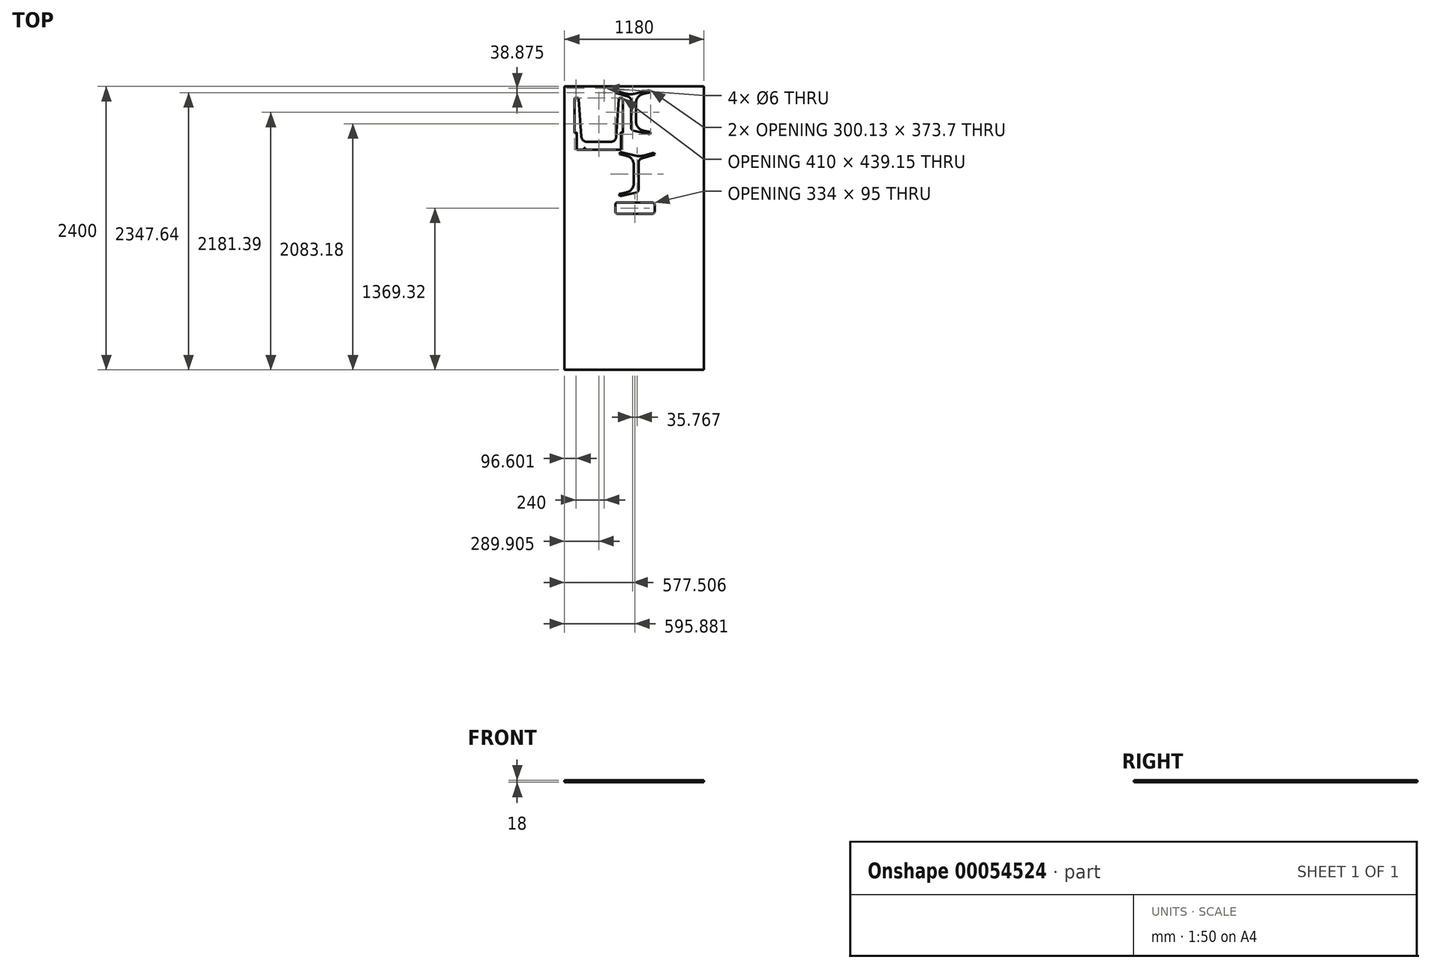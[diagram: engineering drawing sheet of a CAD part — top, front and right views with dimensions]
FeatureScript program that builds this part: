
annotation { "Feature Type Name" : "Feature", "Feature Type Description" : "" }
export const myFeature = defineFeature(function(context is Context, id is Id, definition is map)
    precondition{}
    {
        {
            var Q0;
            Q0=qCreatedBy(makeId("Top.planeOp"),FACE);
            var sketch = newSketch(context, id + "F0", { "sketchPlane" : qUnion([Q0])});
            skArc(sketch, "E0", {"start": v(-2548.4, 1578.94) * mm, "mid": v(-2545.76, 1572.58) * mm, "end": v(-2539.4, 1569.94) * mm});
            skLineSegment(sketch, "E1", {"start": v(-2539.4, 1569.94) * mm, "end": v(-2521.82, 1569.94) * mm});
            skArc(sketch, "E2", {"start": v(-2521.82, 1569.94) * mm, "mid": v(-2515.67, 1572.37) * mm, "end": v(-2512.84, 1578.34) * mm});
            skLineSegment(sketch, "E3", {"start": v(-2512.84, 1578.34) * mm, "end": v(-2491.59, 1896.94) * mm});
            skArc(sketch, "E4", {"start": v(-2491.59, 1896.94) * mm, "mid": v(-2476.37, 1929.04) * mm, "end": v(-2443.33, 1942.1) * mm});
            skLineSegment(sketch, "E5", {"start": v(-2443.33, 1942.1) * mm, "end": v(-2343.4, 1942.1) * mm});
            skLineSegment(sketch, "E6", {"start": v(-2343.4, 1942.1) * mm, "end": v(-2243.47, 1942.1) * mm});
            skArc(sketch, "E7", {"start": v(-2243.47, 1942.1) * mm, "mid": v(-2210.43, 1929.04) * mm, "end": v(-2195.21, 1896.94) * mm});
            skLineSegment(sketch, "E8", {"start": v(-2195.21, 1896.94) * mm, "end": v(-2173.96, 1578.34) * mm});
            skArc(sketch, "E9", {"start": v(-2173.96, 1578.34) * mm, "mid": v(-2171.13, 1572.37) * mm, "end": v(-2164.98, 1569.94) * mm});
            skLineSegment(sketch, "E10", {"start": v(-2164.98, 1569.94) * mm, "end": v(-2147.4, 1569.94) * mm});
            skArc(sketch, "E11", {"start": v(-2147.4, 1569.94) * mm, "mid": v(-2141.03, 1572.58) * mm, "end": v(-2138.4, 1578.94) * mm});
            skLineSegment(sketch, "E12", {"start": v(-2138.4, 1578.94) * mm, "end": v(-2138.4, 1864.94) * mm});
            skLineSegment(sketch, "E13", {"start": v(-2138.4, 1864.94) * mm, "end": v(-2150.74, 1864.94) * mm});
            skArc(sketch, "E14", {"start": v(-2150.74, 1864.94) * mm, "mid": v(-2156.4, 1864.94) * mm, "end": v(-2156.4, 1870.6) * mm});
            skLineSegment(sketch, "E15", {"start": v(-2156.4, 1870.6) * mm, "end": v(-2156.4, 2009.1) * mm});
            skLineSegment(sketch, "E16", {"start": v(-2156.4, 2009.1) * mm, "end": v(-2530.4, 2009.1) * mm});
            skLineSegment(sketch, "E17", {"start": v(-2530.4, 2009.1) * mm, "end": v(-2530.4, 1870.6) * mm});
            skArc(sketch, "E18", {"start": v(-2530.4, 1870.6) * mm, "mid": v(-2530.4, 1864.94) * mm, "end": v(-2536.06, 1864.94) * mm});
            skLineSegment(sketch, "E19", {"start": v(-2536.06, 1864.94) * mm, "end": v(-2548.4, 1864.94) * mm});
            skLineSegment(sketch, "E20", {"start": v(-2548.4, 1864.94) * mm, "end": v(-2548.4, 1578.94) * mm});
            skCircle(sketch, "E21", {"center": v(-1886.18, 1415.07) * mm, "radius": 3 * mm});
            skCircle(sketch, "E22", {"center": v(-2003.5, 1109.65) * mm, "radius": 3 * mm});
            skCircle(sketch, "E23", {"center": v(-1818.83, 1434.38) * mm, "radius": 3 * mm});
            skCircle(sketch, "E24", {"center": v(-2003.5, 1424.41) * mm, "radius": 3 * mm});
            skCircle(sketch, "E25", {"center": v(-1943.68, 1144.84) * mm, "radius": 3 * mm});
            skCircle(sketch, "E26", {"center": v(-2069.06, 1439.55) * mm, "radius": 3 * mm});
            skCircle(sketch, "E27", {"center": v(-1943.68, 1356.02) * mm, "radius": 3 * mm});
            skCircle(sketch, "E28", {"center": v(-2069.06, 1094.52) * mm, "radius": 3 * mm});
            skArc(sketch, "E29", {"start": v(-1949.68, 1112.84) * mm, "mid": v(-1938.52, 1119.88) * mm, "end": v(-1934.18, 1132.33) * mm});
            skLineSegment(sketch, "E30", {"start": v(-1934.18, 1132.33) * mm, "end": v(-1934.18, 1361.8) * mm});
            skArc(sketch, "E31", {"start": v(-1934.18, 1361.8) * mm, "mid": v(-1926.12, 1385.87) * mm, "end": v(-1905.2, 1400.25) * mm});
            skLineSegment(sketch, "E32", {"start": v(-1905.2, 1400.25) * mm, "end": v(-1796.66, 1431.37) * mm});
            skLineSegment(sketch, "E33", {"start": v(-1796.66, 1431.37) * mm, "end": v(-1801.62, 1448.68) * mm});
            skLineSegment(sketch, "E34", {"start": v(-1801.62, 1448.68) * mm, "end": v(-1883.4, 1425.23) * mm});
            skArc(sketch, "E35", {"start": v(-1883.4, 1425.23) * mm, "mid": v(-1920.82, 1419.47) * mm, "end": v(-1958.49, 1423.26) * mm});
            skLineSegment(sketch, "E36", {"start": v(-1958.49, 1423.26) * mm, "end": v(-2089.54, 1453.52) * mm});
            skLineSegment(sketch, "E37", {"start": v(-2089.54, 1453.52) * mm, "end": v(-2093.58, 1435.98) * mm});
            skLineSegment(sketch, "E38", {"start": v(-2093.58, 1435.98) * mm, "end": v(-2036.18, 1422.72) * mm});
            skArc(sketch, "E39", {"start": v(-2036.18, 1422.72) * mm, "mid": v(-1991.57, 1394.58) * mm, "end": v(-1974.18, 1344.77) * mm});
            skLineSegment(sketch, "E40", {"start": v(-1974.18, 1344.77) * mm, "end": v(-1974.18, 1189.3) * mm});
            skArc(sketch, "E41", {"start": v(-1974.18, 1189.3) * mm, "mid": v(-1991.57, 1139.5) * mm, "end": v(-2036.18, 1111.34) * mm});
            skLineSegment(sketch, "E42", {"start": v(-2036.18, 1111.34) * mm, "end": v(-2096.8, 1097.35) * mm});
            skLineSegment(sketch, "E43", {"start": v(-2096.8, 1097.35) * mm, "end": v(-2092.74, 1079.81) * mm});
            skLineSegment(sketch, "E44", {"start": v(-2092.74, 1079.81) * mm, "end": v(-1949.68, 1112.84) * mm});
            skLineSegment(sketch, "E45", {"start": v(-2203.5, 942.03) * mm, "end": v(-2186, 942.03) * mm});
            skLineSegment(sketch, "E46", {"start": v(-2186, 942.03) * mm, "end": v(-2186, 1249.22) * mm});
            skArc(sketch, "E47", {"start": v(-2186, 1249.22) * mm, "mid": v(-2194.79, 1270.43) * mm, "end": v(-2216, 1279.22) * mm});
            skLineSegment(sketch, "E48", {"start": v(-2216, 1279.22) * mm, "end": v(-2530, 1279.22) * mm});
            skArc(sketch, "E49", {"start": v(-2530, 1279.22) * mm, "mid": v(-2551.21, 1270.43) * mm, "end": v(-2560, 1249.22) * mm});
            skLineSegment(sketch, "E50", {"start": v(-2560, 1249.22) * mm, "end": v(-2560, 942.03) * mm});
            skLineSegment(sketch, "E51", {"start": v(-2560, 942.03) * mm, "end": v(-2542.5, 942.03) * mm});
            skArc(sketch, "E52", {"start": v(-2542.5, 942.03) * mm, "mid": v(-2540.38, 941.15) * mm, "end": v(-2539.5, 939.03) * mm});
            skLineSegment(sketch, "E53", {"start": v(-2539.5, 939.03) * mm, "end": v(-2539.5, 919.22) * mm});
            skArc(sketch, "E54", {"start": v(-2539.5, 919.22) * mm, "mid": v(-2533.64, 905.08) * mm, "end": v(-2519.5, 899.22) * mm});
            skLineSegment(sketch, "E55", {"start": v(-2519.5, 899.22) * mm, "end": v(-2226.5, 899.22) * mm});
            skArc(sketch, "E56", {"start": v(-2226.5, 899.22) * mm, "mid": v(-2212.36, 905.08) * mm, "end": v(-2206.5, 919.22) * mm});
            skLineSegment(sketch, "E57", {"start": v(-2206.5, 919.22) * mm, "end": v(-2206.5, 939.03) * mm});
            skArc(sketch, "E58", {"start": v(-2206.5, 939.03) * mm, "mid": v(-2205.62, 941.15) * mm, "end": v(-2203.5, 942.03) * mm});
            skLineSegment(sketch, "E59", {"start": v(-2131.12, 1005.82) * mm, "end": v(-2131.12, 950.82) * mm});
            skArc(sketch, "E60", {"start": v(-2131.12, 950.82) * mm, "mid": v(-2125.26, 936.68) * mm, "end": v(-2111.12, 930.82) * mm});
            skLineSegment(sketch, "E61", {"start": v(-2111.12, 930.82) * mm, "end": v(-1817.12, 930.82) * mm});
            skArc(sketch, "E62", {"start": v(-1817.12, 930.82) * mm, "mid": v(-1802.98, 936.68) * mm, "end": v(-1797.12, 950.82) * mm});
            skLineSegment(sketch, "E63", {"start": v(-1797.12, 950.82) * mm, "end": v(-1797.12, 1005.82) * mm});
            skArc(sketch, "E64", {"start": v(-1797.12, 1005.82) * mm, "mid": v(-1802.98, 1019.96) * mm, "end": v(-1817.12, 1025.82) * mm});
            skLineSegment(sketch, "E65", {"start": v(-1817.12, 1025.82) * mm, "end": v(-2111.12, 1025.82) * mm});
            skArc(sketch, "E66", {"start": v(-2111.12, 1025.82) * mm, "mid": v(-2125.26, 1019.96) * mm, "end": v(-2131.12, 1005.82) * mm});
            skLineSegment(sketch, "E67", {"start": v(-2507, 1456.47) * mm, "end": v(-2491.55, 1389.58) * mm});
            skLineSegment(sketch, "E68", {"start": v(-2491.55, 1389.58) * mm, "end": v(-2218.96, 1389.58) * mm});
            skLineSegment(sketch, "E69", {"start": v(-2218.96, 1389.58) * mm, "end": v(-2203.52, 1456.47) * mm});
            skLineSegment(sketch, "E70", {"start": v(-2203.52, 1456.47) * mm, "end": v(-2213.65, 1458.8) * mm});
            skArc(sketch, "E71", {"start": v(-2213.65, 1458.8) * mm, "mid": v(-2219.1, 1458.43) * mm, "end": v(-2223.44, 1455.07) * mm});
            skLineSegment(sketch, "E72", {"start": v(-2223.44, 1455.07) * mm, "end": v(-2245.43, 1424) * mm});
            skArc(sketch, "E73", {"start": v(-2245.43, 1424) * mm, "mid": v(-2253.38, 1417.07) * mm, "end": v(-2263.62, 1414.58) * mm});
            skLineSegment(sketch, "E74", {"start": v(-2263.62, 1414.58) * mm, "end": v(-2355.26, 1414.58) * mm});
            skLineSegment(sketch, "E75", {"start": v(-2355.26, 1414.58) * mm, "end": v(-2446.9, 1414.58) * mm});
            skArc(sketch, "E76", {"start": v(-2446.9, 1414.58) * mm, "mid": v(-2457.13, 1417.07) * mm, "end": v(-2465.08, 1424) * mm});
            skLineSegment(sketch, "E77", {"start": v(-2465.08, 1424) * mm, "end": v(-2487.08, 1455.07) * mm});
            skArc(sketch, "E78", {"start": v(-2487.08, 1455.07) * mm, "mid": v(-2491.4, 1458.43) * mm, "end": v(-2496.87, 1458.8) * mm});
            skLineSegment(sketch, "E79", {"start": v(-2496.87, 1458.8) * mm, "end": v(-2507, 1456.47) * mm});
            skArc(sketch, "E80", {"start": v(-1979.54, 1636.57) * mm, "mid": v(-1990.7, 1643.6) * mm, "end": v(-1995.05, 1656.05) * mm});
            skLineSegment(sketch, "E81", {"start": v(-1995.05, 1656.05) * mm, "end": v(-1995.05, 1885.52) * mm});
            skArc(sketch, "E82", {"start": v(-1995.05, 1885.52) * mm, "mid": v(-2003.1, 1909.6) * mm, "end": v(-2024.02, 1923.97) * mm});
            skLineSegment(sketch, "E83", {"start": v(-2024.02, 1923.97) * mm, "end": v(-2132.56, 1955.1) * mm});
            skLineSegment(sketch, "E84", {"start": v(-2132.56, 1955.1) * mm, "end": v(-2127.6, 1972.4) * mm});
            skLineSegment(sketch, "E85", {"start": v(-2127.6, 1972.4) * mm, "end": v(-2045.82, 1948.95) * mm});
            skArc(sketch, "E86", {"start": v(-2045.82, 1948.95) * mm, "mid": v(-2008.4, 1943.2) * mm, "end": v(-1970.73, 1946.98) * mm});
            skLineSegment(sketch, "E87", {"start": v(-1970.73, 1946.98) * mm, "end": v(-1839.69, 1977.24) * mm});
            skLineSegment(sketch, "E88", {"start": v(-1839.69, 1977.24) * mm, "end": v(-1835.64, 1959.7) * mm});
            skLineSegment(sketch, "E89", {"start": v(-1835.64, 1959.7) * mm, "end": v(-1893.04, 1946.45) * mm});
            skArc(sketch, "E90", {"start": v(-1893.04, 1946.45) * mm, "mid": v(-1937.65, 1918.3) * mm, "end": v(-1955.05, 1868.5) * mm});
            skLineSegment(sketch, "E91", {"start": v(-1955.05, 1868.5) * mm, "end": v(-1955.05, 1713.02) * mm});
            skArc(sketch, "E92", {"start": v(-1955.05, 1713.02) * mm, "mid": v(-1937.65, 1663.22) * mm, "end": v(-1893.04, 1635.07) * mm});
            skLineSegment(sketch, "E93", {"start": v(-1893.04, 1635.07) * mm, "end": v(-1832.43, 1621.07) * mm});
            skLineSegment(sketch, "E94", {"start": v(-1832.43, 1621.07) * mm, "end": v(-1836.48, 1603.54) * mm});
            skLineSegment(sketch, "E95", {"start": v(-1836.48, 1603.54) * mm, "end": v(-1979.54, 1636.57) * mm});
            skCircle(sketch, "E96", {"center": v(-1860.16, 1963.27) * mm, "radius": 3 * mm});
            skCircle(sketch, "E97", {"center": v(-1925.73, 1948.14) * mm, "radius": 3 * mm});
            skCircle(sketch, "E98", {"center": v(-2110.4, 1958.1) * mm, "radius": 3 * mm});
            skCircle(sketch, "E99", {"center": v(-1985.55, 1879.74) * mm, "radius": 3 * mm});
            skCircle(sketch, "E100", {"center": v(-1985.55, 1668.56) * mm, "radius": 3 * mm});
            skCircle(sketch, "E101", {"center": v(-1925.73, 1633.38) * mm, "radius": 3 * mm});
            skCircle(sketch, "E102", {"center": v(-1860.16, 1618.24) * mm, "radius": 3 * mm});
            skCircle(sketch, "E103", {"center": v(-2043.04, 1938.8) * mm, "radius": 3 * mm});
            skCircle(sketch, "E104", {"center": v(-2223.4, 1956.64) * mm, "radius": 3 * mm});
            skCircle(sketch, "E105", {"center": v(-2463.4, 1995.52) * mm, "radius": 3 * mm});
            skCircle(sketch, "E106", {"center": v(-2463.4, 1956.64) * mm, "radius": 3 * mm});
            skCircle(sketch, "E107", {"center": v(-2223.4, 1995.52) * mm, "radius": 3 * mm});
            skCircle(sketch, "E108", {"center": v(-2390.1, 1486.18) * mm, "radius": 3 * mm});
            skCircle(sketch, "E109", {"center": v(-2150.1, 1525.06) * mm, "radius": 3 * mm});
            skCircle(sketch, "E110", {"center": v(-2150.1, 1486.18) * mm, "radius": 3 * mm});
            skCircle(sketch, "E111", {"center": v(-2390.1, 1525.06) * mm, "radius": 3 * mm});
            skArc(sketch, "E112", {"start": v(-2065.1, 1902.75) * mm, "mid": v(-2067.73, 1909.12) * mm, "end": v(-2074.1, 1911.75) * mm});
            skLineSegment(sketch, "E113", {"start": v(-2074.1, 1911.75) * mm, "end": v(-2091.68, 1911.75) * mm});
            skArc(sketch, "E114", {"start": v(-2091.68, 1911.75) * mm, "mid": v(-2097.82, 1909.33) * mm, "end": v(-2100.66, 1903.35) * mm});
            skLineSegment(sketch, "E115", {"start": v(-2100.66, 1903.35) * mm, "end": v(-2121.9, 1584.75) * mm});
            skArc(sketch, "E116", {"start": v(-2121.9, 1584.75) * mm, "mid": v(-2137.12, 1552.65) * mm, "end": v(-2170.16, 1539.6) * mm});
            skLineSegment(sketch, "E117", {"start": v(-2170.16, 1539.6) * mm, "end": v(-2270.1, 1539.6) * mm});
            skLineSegment(sketch, "E118", {"start": v(-2270.1, 1539.6) * mm, "end": v(-2370.03, 1539.6) * mm});
            skArc(sketch, "E119", {"start": v(-2370.03, 1539.6) * mm, "mid": v(-2403.07, 1552.65) * mm, "end": v(-2418.28, 1584.75) * mm});
            skLineSegment(sketch, "E120", {"start": v(-2418.28, 1584.75) * mm, "end": v(-2439.53, 1903.35) * mm});
            skArc(sketch, "E121", {"start": v(-2439.53, 1903.35) * mm, "mid": v(-2442.37, 1909.33) * mm, "end": v(-2448.51, 1911.75) * mm});
            skLineSegment(sketch, "E122", {"start": v(-2448.51, 1911.75) * mm, "end": v(-2466.1, 1911.75) * mm});
            skArc(sketch, "E123", {"start": v(-2466.1, 1911.75) * mm, "mid": v(-2472.46, 1909.12) * mm, "end": v(-2475.1, 1902.75) * mm});
            skLineSegment(sketch, "E124", {"start": v(-2475.1, 1902.75) * mm, "end": v(-2475.1, 1616.76) * mm});
            skLineSegment(sketch, "E125", {"start": v(-2475.1, 1616.76) * mm, "end": v(-2462.75, 1616.76) * mm});
            skArc(sketch, "E126", {"start": v(-2462.75, 1616.76) * mm, "mid": v(-2457.1, 1616.76) * mm, "end": v(-2457.1, 1611.1) * mm});
            skLineSegment(sketch, "E127", {"start": v(-2457.1, 1611.1) * mm, "end": v(-2457.1, 1472.6) * mm});
            skLineSegment(sketch, "E128", {"start": v(-2457.1, 1472.6) * mm, "end": v(-2083.1, 1472.6) * mm});
            skLineSegment(sketch, "E129", {"start": v(-2083.1, 1472.6) * mm, "end": v(-2083.1, 1611.1) * mm});
            skArc(sketch, "E130", {"start": v(-2083.1, 1611.1) * mm, "mid": v(-2083.1, 1616.76) * mm, "end": v(-2077.44, 1616.76) * mm});
            skLineSegment(sketch, "E131", {"start": v(-2077.44, 1616.76) * mm, "end": v(-2065.1, 1616.76) * mm});
            skLineSegment(sketch, "E132", {"start": v(-2065.1, 1616.76) * mm, "end": v(-2065.1, 1902.75) * mm});
            skLineSegment(sketch, "E133", {"start": v(-2151.12, 1322.1) * mm, "end": v(-2131.12, 1322.1) * mm});
            skLineSegment(sketch, "E134", {"start": v(-2131.12, 1322.1) * mm, "end": v(-2131.12, 1080.82) * mm});
            skArc(sketch, "E135", {"start": v(-2131.12, 1080.82) * mm, "mid": v(-2125.26, 1066.68) * mm, "end": v(-2111.12, 1060.82) * mm});
            skLineSegment(sketch, "E136", {"start": v(-2111.12, 1060.82) * mm, "end": v(-1817.12, 1060.82) * mm});
            skArc(sketch, "E137", {"start": v(-1817.12, 1060.82) * mm, "mid": v(-1802.98, 1066.68) * mm, "end": v(-1797.12, 1080.82) * mm});
            skLineSegment(sketch, "E138", {"start": v(-1797.12, 1080.82) * mm, "end": v(-1797.12, 1322.1) * mm});
            skLineSegment(sketch, "E139", {"start": v(-1797.12, 1322.1) * mm, "end": v(-1777.12, 1322.1) * mm});
            skLineSegment(sketch, "E140", {"start": v(-1777.12, 1322.1) * mm, "end": v(-1777.12, 1158.18) * mm});
            skArc(sketch, "E141", {"start": v(-1777.12, 1158.18) * mm, "mid": v(-1777.12, 1152.53) * mm, "end": v(-1771.46, 1152.53) * mm});
            skLineSegment(sketch, "E142", {"start": v(-1771.46, 1152.53) * mm, "end": v(-1759.12, 1152.53) * mm});
            skLineSegment(sketch, "E143", {"start": v(-1759.12, 1152.53) * mm, "end": v(-1759.12, 930.82) * mm});
            skArc(sketch, "E144", {"start": v(-1759.12, 930.82) * mm, "mid": v(-1769.37, 906.07) * mm, "end": v(-1794.12, 895.82) * mm});
            skLineSegment(sketch, "E145", {"start": v(-1794.12, 895.82) * mm, "end": v(-2134.12, 895.82) * mm});
            skArc(sketch, "E146", {"start": v(-2134.12, 895.82) * mm, "mid": v(-2158.87, 906.07) * mm, "end": v(-2169.12, 930.82) * mm});
            skLineSegment(sketch, "E147", {"start": v(-2169.12, 930.82) * mm, "end": v(-2169.12, 1152.53) * mm});
            skLineSegment(sketch, "E148", {"start": v(-2169.12, 1152.53) * mm, "end": v(-2156.78, 1152.53) * mm});
            skArc(sketch, "E149", {"start": v(-2156.78, 1152.53) * mm, "mid": v(-2151.12, 1152.53) * mm, "end": v(-2151.12, 1158.18) * mm});
            skLineSegment(sketch, "E150", {"start": v(-2151.12, 1158.18) * mm, "end": v(-2151.12, 1322.1) * mm});
            skLineSegment(sketch, "E151", {"start": v(-2790, -2229) * mm, "end": v(-2790, -1929) * mm});
            skLineSegment(sketch, "E152", {"start": v(-2790, -1929) * mm, "end": v(-3090, -1929) * mm});
            skLineSegment(sketch, "E153", {"start": v(-2790, 2229) * mm, "end": v(3090, 2229) * mm, "construction": true});
            skLineSegment(sketch, "E154", {"start": v(3090, 2229) * mm, "end": v(3090, -1929) * mm});
            skLineSegment(sketch, "E155", {"start": v(3090, -1929) * mm, "end": v(-2790, -1929) * mm});
            skLineSegment(sketch, "E156", {"start": v(-2790, -1929) * mm, "end": v(-2790, 2229) * mm});
            skLineSegment(sketch, "E157", {"start": v(-2580, 2029) * mm, "end": v(-1360, 2029) * mm, "construction": true});
            skLineSegment(sketch, "E158", {"start": v(-1360, 2029) * mm, "end": v(-1360, -411) * mm});
            skLineSegment(sketch, "E159", {"start": v(-1360, -411) * mm, "end": v(-2580, -411) * mm});
            skLineSegment(sketch, "E160", {"start": v(-2580, -411) * mm, "end": v(-2580, 2029) * mm});
            skLineSegment(sketch, "E161", {"start": v(-960, 2029) * mm, "end": v(260, 2029) * mm});
            skLineSegment(sketch, "E162", {"start": v(260, 2029) * mm, "end": v(260, -411) * mm});
            skLineSegment(sketch, "E163", {"start": v(260, -411) * mm, "end": v(-960, -411) * mm});
            skLineSegment(sketch, "E164", {"start": v(-960, -411) * mm, "end": v(-960, 2029) * mm});
            skLineSegment(sketch, "E165", {"start": v(660, 2029) * mm, "end": v(1880, 2029) * mm});
            skLineSegment(sketch, "E166", {"start": v(1880, 2029) * mm, "end": v(1880, -411) * mm});
            skLineSegment(sketch, "E167", {"start": v(1880, -411) * mm, "end": v(660, -411) * mm});
            skLineSegment(sketch, "E168", {"start": v(660, -411) * mm, "end": v(660, 2029) * mm});
            skLineSegment(sketch, "E169", {"start": v(-1160, -585.8) * mm, "end": v(-1160, 2079) * mm});
            skLineSegment(sketch, "E170", {"start": v(-2580, -411) * mm, "end": v(-2580, 2029) * mm, "construction": true});
            skLineSegment(sketch, "E171", {"start": v(-2560, 2009) * mm, "end": v(-1380, 2009) * mm, "construction": true});
            skLineSegment(sketch, "E172", {"start": v(-1380, 2009) * mm, "end": v(-1380, -391) * mm});
            skLineSegment(sketch, "E173", {"start": v(-1380, -391) * mm, "end": v(-2560, -391) * mm});
            skLineSegment(sketch, "E174", {"start": v(-2560, -391) * mm, "end": v(-2560, 2009) * mm, "construction": true});
            skLineSegment(sketch, "E175", {"start": v(-940, 2009) * mm, "end": v(240, 2009) * mm});
            skLineSegment(sketch, "E176", {"start": v(240, 2009) * mm, "end": v(240, -391) * mm});
            skLineSegment(sketch, "E177", {"start": v(240, -391) * mm, "end": v(-940, -391) * mm});
            skLineSegment(sketch, "E178", {"start": v(-940, -391) * mm, "end": v(-940, 2009) * mm});
            skLineSegment(sketch, "E179", {"start": v(680, 2009) * mm, "end": v(1860, 2009) * mm});
            skLineSegment(sketch, "E180", {"start": v(1860, 2009) * mm, "end": v(1860, -391) * mm});
            skLineSegment(sketch, "E181", {"start": v(1860, -391) * mm, "end": v(680, -391) * mm});
            skLineSegment(sketch, "E182", {"start": v(680, -391) * mm, "end": v(680, 2009) * mm});
            skLineSegment(sketch, "E183", {"start": v(2149.33, 1968.96) * mm, "end": v(2149.33, 1941.15) * mm});
            skArc(sketch, "E184", {"start": v(2149.33, 1941.15) * mm, "mid": v(2131.14, 1922.95) * mm, "end": v(2112.94, 1941.15) * mm});
            skLineSegment(sketch, "E185", {"start": v(2112.94, 1941.15) * mm, "end": v(2112.94, 1968.96) * mm});
            skArc(sketch, "E186", {"start": v(2112.94, 1968.96) * mm, "mid": v(2131.14, 1987.16) * mm, "end": v(2149.33, 1968.96) * mm});
            skLineSegment(sketch, "E187", {"start": v(2105, 1968.96) * mm, "end": v(2105, 1941.15) * mm});
            skArc(sketch, "E188", {"start": v(2105, 1941.15) * mm, "mid": v(2131.14, 1915.01) * mm, "end": v(2157.27, 1941.15) * mm});
            skLineSegment(sketch, "E189", {"start": v(2157.27, 1941.15) * mm, "end": v(2157.27, 1968.96) * mm});
            skArc(sketch, "E190", {"start": v(2157.27, 1968.96) * mm, "mid": v(2131.14, 1995.1) * mm, "end": v(2105, 1968.96) * mm});
            skArc(sketch, "E191", {"start": v(2191.3, 1968.96) * mm, "mid": v(2209.5, 1987.16) * mm, "end": v(2227.7, 1968.96) * mm});
            skLineSegment(sketch, "E192", {"start": v(2227.7, 1968.96) * mm, "end": v(2227.7, 1941.15) * mm});
            skArc(sketch, "E193", {"start": v(2227.7, 1941.15) * mm, "mid": v(2209.5, 1922.95) * mm, "end": v(2191.3, 1941.15) * mm});
            skLineSegment(sketch, "E194", {"start": v(2191.3, 1941.15) * mm, "end": v(2191.3, 1968.96) * mm});
            skArc(sketch, "E195", {"start": v(2235.64, 1968.96) * mm, "mid": v(2219.69, 1993.03) * mm, "end": v(2191.3, 1987.72) * mm});
            skLineSegment(sketch, "E196", {"start": v(2191.3, 1987.72) * mm, "end": v(2191.3, 1991.13) * mm});
            skArc(sketch, "E197", {"start": v(2191.3, 1991.13) * mm, "mid": v(2187.34, 1995.1) * mm, "end": v(2183.37, 1991.13) * mm});
            skLineSegment(sketch, "E198", {"start": v(2183.37, 1991.13) * mm, "end": v(2183.37, 1885.07) * mm});
            skArc(sketch, "E199", {"start": v(2183.37, 1885.07) * mm, "mid": v(2187.34, 1881.1) * mm, "end": v(2191.3, 1885.07) * mm});
            skLineSegment(sketch, "E200", {"start": v(2191.3, 1885.07) * mm, "end": v(2191.3, 1922.39) * mm});
            skArc(sketch, "E201", {"start": v(2191.3, 1922.39) * mm, "mid": v(2219.69, 1917.08) * mm, "end": v(2235.64, 1941.15) * mm});
            skLineSegment(sketch, "E202", {"start": v(2235.64, 1941.15) * mm, "end": v(2235.64, 1968.96) * mm});
            skLineSegment(sketch, "E203", {"start": v(2304.36, 1959.07) * mm, "end": v(2267.96, 1959.07) * mm});
            skLineSegment(sketch, "E204", {"start": v(2267.96, 1959.07) * mm, "end": v(2267.96, 1968.96) * mm});
            skArc(sketch, "E205", {"start": v(2267.96, 1968.96) * mm, "mid": v(2286.16, 1987.16) * mm, "end": v(2304.36, 1968.96) * mm});
            skLineSegment(sketch, "E206", {"start": v(2304.36, 1968.96) * mm, "end": v(2304.36, 1959.07) * mm});
            skArc(sketch, "E207", {"start": v(2312.3, 1968.96) * mm, "mid": v(2286.16, 1995.1) * mm, "end": v(2260.03, 1968.96) * mm});
            skLineSegment(sketch, "E208", {"start": v(2260.03, 1968.96) * mm, "end": v(2260.03, 1941.15) * mm});
            skArc(sketch, "E209", {"start": v(2260.03, 1941.15) * mm, "mid": v(2281.63, 1915.4) * mm, "end": v(2310.72, 1932.22) * mm});
            skArc(sketch, "E210", {"start": v(2310.72, 1932.22) * mm, "mid": v(2308.35, 1937.3) * mm, "end": v(2303.26, 1934.93) * mm});
            skArc(sketch, "E211", {"start": v(2303.26, 1934.93) * mm, "mid": v(2283, 1923.22) * mm, "end": v(2267.96, 1941.15) * mm});
            skLineSegment(sketch, "E212", {"start": v(2267.96, 1941.15) * mm, "end": v(2267.96, 1951.14) * mm});
            skLineSegment(sketch, "E213", {"start": v(2267.96, 1951.14) * mm, "end": v(2308.33, 1951.14) * mm});
            skArc(sketch, "E214", {"start": v(2308.33, 1951.14) * mm, "mid": v(2311.13, 1952.3) * mm, "end": v(2312.3, 1955.1) * mm});
            skLineSegment(sketch, "E215", {"start": v(2312.3, 1955.1) * mm, "end": v(2312.3, 1968.96) * mm});
            skArc(sketch, "E216", {"start": v(2388.85, 1968.96) * mm, "mid": v(2372.9, 1993.03) * mm, "end": v(2344.52, 1987.72) * mm});
            skLineSegment(sketch, "E217", {"start": v(2344.52, 1987.72) * mm, "end": v(2344.52, 1991.13) * mm});
            skArc(sketch, "E218", {"start": v(2344.52, 1991.13) * mm, "mid": v(2340.55, 1995.1) * mm, "end": v(2336.58, 1991.13) * mm});
            skLineSegment(sketch, "E219", {"start": v(2336.58, 1991.13) * mm, "end": v(2336.58, 1918.98) * mm});
            skArc(sketch, "E220", {"start": v(2336.58, 1918.98) * mm, "mid": v(2340.55, 1915.01) * mm, "end": v(2344.52, 1918.98) * mm});
            skLineSegment(sketch, "E221", {"start": v(2344.52, 1918.98) * mm, "end": v(2344.52, 1968.96) * mm});
            skArc(sketch, "E222", {"start": v(2344.52, 1968.96) * mm, "mid": v(2362.72, 1987.16) * mm, "end": v(2380.92, 1968.96) * mm});
            skLineSegment(sketch, "E223", {"start": v(2380.92, 1968.96) * mm, "end": v(2380.92, 1918.98) * mm});
            skArc(sketch, "E224", {"start": v(2380.92, 1918.98) * mm, "mid": v(2384.89, 1915.01) * mm, "end": v(2388.85, 1918.98) * mm});
            skLineSegment(sketch, "E225", {"start": v(2388.85, 1918.98) * mm, "end": v(2388.85, 1968.96) * mm});
            skArc(sketch, "E226", {"start": v(2457.36, 1941.15) * mm, "mid": v(2439.16, 1922.95) * mm, "end": v(2420.96, 1941.15) * mm});
            skLineSegment(sketch, "E227", {"start": v(2420.96, 1941.15) * mm, "end": v(2420.96, 1968.96) * mm});
            skArc(sketch, "E228", {"start": v(2420.96, 1968.96) * mm, "mid": v(2439.16, 1987.16) * mm, "end": v(2457.36, 1968.96) * mm});
            skLineSegment(sketch, "E229", {"start": v(2457.36, 1968.96) * mm, "end": v(2457.36, 1941.15) * mm});
            skArc(sketch, "E230", {"start": v(2413.02, 1941.15) * mm, "mid": v(2428.98, 1917.08) * mm, "end": v(2457.36, 1922.39) * mm});
            skLineSegment(sketch, "E231", {"start": v(2457.36, 1922.39) * mm, "end": v(2457.36, 1918.98) * mm});
            skArc(sketch, "E232", {"start": v(2457.36, 1918.98) * mm, "mid": v(2461.33, 1915.01) * mm, "end": v(2465.3, 1918.98) * mm});
            skLineSegment(sketch, "E233", {"start": v(2465.3, 1918.98) * mm, "end": v(2465.3, 2025.03) * mm});
            skArc(sketch, "E234", {"start": v(2465.3, 2025.03) * mm, "mid": v(2461.33, 2029) * mm, "end": v(2457.36, 2025.03) * mm});
            skLineSegment(sketch, "E235", {"start": v(2457.36, 2025.03) * mm, "end": v(2457.36, 1987.72) * mm});
            skArc(sketch, "E236", {"start": v(2457.36, 1987.72) * mm, "mid": v(2428.98, 1993.03) * mm, "end": v(2413.02, 1968.96) * mm});
            skLineSegment(sketch, "E237", {"start": v(2413.02, 1968.96) * mm, "end": v(2413.02, 1941.15) * mm});
            skLineSegment(sketch, "E238", {"start": v(2538.98, 1959.07) * mm, "end": v(2502.58, 1959.07) * mm});
            skLineSegment(sketch, "E239", {"start": v(2502.58, 1959.07) * mm, "end": v(2502.58, 1968.96) * mm});
            skArc(sketch, "E240", {"start": v(2502.58, 1968.96) * mm, "mid": v(2520.78, 1987.16) * mm, "end": v(2538.98, 1968.96) * mm});
            skLineSegment(sketch, "E241", {"start": v(2538.98, 1968.96) * mm, "end": v(2538.98, 1959.07) * mm});
            skArc(sketch, "E242", {"start": v(2546.92, 1968.96) * mm, "mid": v(2520.78, 1995.1) * mm, "end": v(2494.65, 1968.96) * mm});
            skLineSegment(sketch, "E243", {"start": v(2494.65, 1968.96) * mm, "end": v(2494.65, 1941.15) * mm});
            skArc(sketch, "E244", {"start": v(2494.65, 1941.15) * mm, "mid": v(2516.25, 1915.4) * mm, "end": v(2545.34, 1932.22) * mm});
            skArc(sketch, "E245", {"start": v(2545.34, 1932.22) * mm, "mid": v(2542.97, 1937.3) * mm, "end": v(2537.88, 1934.93) * mm});
            skArc(sketch, "E246", {"start": v(2537.88, 1934.93) * mm, "mid": v(2517.62, 1923.22) * mm, "end": v(2502.58, 1941.15) * mm});
            skLineSegment(sketch, "E247", {"start": v(2502.58, 1941.15) * mm, "end": v(2502.58, 1951.14) * mm});
            skLineSegment(sketch, "E248", {"start": v(2502.58, 1951.14) * mm, "end": v(2542.95, 1951.14) * mm});
            skArc(sketch, "E249", {"start": v(2542.95, 1951.14) * mm, "mid": v(2545.75, 1952.3) * mm, "end": v(2546.92, 1955.1) * mm});
            skLineSegment(sketch, "E250", {"start": v(2546.92, 1955.1) * mm, "end": v(2546.92, 1968.96) * mm});
            skArc(sketch, "E251", {"start": v(2610.13, 1991.29) * mm, "mid": v(2607.92, 1992.38) * mm, "end": v(2605.63, 1993.27) * mm});
            skArc(sketch, "E252", {"start": v(2605.63, 1993.27) * mm, "mid": v(2603.26, 1993.95) * mm, "end": v(2600.85, 1994.45) * mm});
            skArc(sketch, "E253", {"start": v(2600.85, 1994.45) * mm, "mid": v(2597.2, 1994.9) * mm, "end": v(2593.54, 1995.04) * mm});
            skArc(sketch, "E254", {"start": v(2593.54, 1995.04) * mm, "mid": v(2587.5, 1994.47) * mm, "end": v(2581.66, 1992.77) * mm});
            skArc(sketch, "E255", {"start": v(2581.66, 1992.77) * mm, "mid": v(2578.6, 1991.3) * mm, "end": v(2575.8, 1989.4) * mm});
            skArc(sketch, "E256", {"start": v(2575.8, 1989.4) * mm, "mid": v(2574.4, 1988.2) * mm, "end": v(2573.13, 1986.88) * mm});
            skArc(sketch, "E257", {"start": v(2573.13, 1986.88) * mm, "mid": v(2572.07, 1985.55) * mm, "end": v(2571.14, 1984.13) * mm});
            skArc(sketch, "E258", {"start": v(2571.14, 1984.13) * mm, "mid": v(2570.1, 1981.92) * mm, "end": v(2569.38, 1979.59) * mm});
            skArc(sketch, "E259", {"start": v(2569.38, 1979.59) * mm, "mid": v(2570.18, 1968.82) * mm, "end": v(2576.93, 1960.38) * mm});
            skArc(sketch, "E260", {"start": v(2576.93, 1960.38) * mm, "mid": v(2579.38, 1958.9) * mm, "end": v(2581.98, 1957.7) * mm});
            skArc(sketch, "E261", {"start": v(2581.98, 1957.7) * mm, "mid": v(2585.47, 1956.45) * mm, "end": v(2589.05, 1955.5) * mm});
            skArc(sketch, "E262", {"start": v(2589.05, 1955.5) * mm, "mid": v(2593.24, 1954.56) * mm, "end": v(2597.42, 1953.55) * mm});
            skArc(sketch, "E263", {"start": v(2597.42, 1953.55) * mm, "mid": v(2601.09, 1952.53) * mm, "end": v(2604.69, 1951.29) * mm});
            skArc(sketch, "E264", {"start": v(2604.69, 1951.29) * mm, "mid": v(2608.07, 1949.46) * mm, "end": v(2610.85, 1946.81) * mm});
            skArc(sketch, "E265", {"start": v(2610.85, 1946.81) * mm, "mid": v(2611.78, 1945.42) * mm, "end": v(2612.43, 1943.88) * mm});
            skArc(sketch, "E266", {"start": v(2612.43, 1943.88) * mm, "mid": v(2613.25, 1938.78) * mm, "end": v(2612.55, 1933.66) * mm});
            skArc(sketch, "E267", {"start": v(2612.55, 1933.66) * mm, "mid": v(2610.27, 1929.3) * mm, "end": v(2606.48, 1926.15) * mm});
            skArc(sketch, "E268", {"start": v(2606.48, 1926.15) * mm, "mid": v(2594.98, 1922.94) * mm, "end": v(2583.21, 1924.9) * mm});
            skArc(sketch, "E269", {"start": v(2583.21, 1924.9) * mm, "mid": v(2577.34, 1928.7) * mm, "end": v(2573.28, 1934.37) * mm});
            skArc(sketch, "E270", {"start": v(2573.28, 1934.37) * mm, "mid": v(2568, 1936.31) * mm, "end": v(2566.07, 1931.05) * mm});
            skArc(sketch, "E271", {"start": v(2566.07, 1931.05) * mm, "mid": v(2571.86, 1922.95) * mm, "end": v(2580.23, 1917.55) * mm});
            skArc(sketch, "E272", {"start": v(2580.23, 1917.55) * mm, "mid": v(2595.4, 1915.01) * mm, "end": v(2610.23, 1919.16) * mm});
            skArc(sketch, "E273", {"start": v(2610.23, 1919.16) * mm, "mid": v(2616.44, 1924.3) * mm, "end": v(2620.17, 1931.44) * mm});
            skArc(sketch, "E274", {"start": v(2620.17, 1931.44) * mm, "mid": v(2621.18, 1938.87) * mm, "end": v(2620, 1946.28) * mm});
            skArc(sketch, "E275", {"start": v(2620, 1946.28) * mm, "mid": v(2618.77, 1949.18) * mm, "end": v(2617.03, 1951.8) * mm});
            skArc(sketch, "E276", {"start": v(2617.03, 1951.8) * mm, "mid": v(2612.73, 1955.88) * mm, "end": v(2607.51, 1958.7) * mm});
            skArc(sketch, "E277", {"start": v(2607.51, 1958.7) * mm, "mid": v(2603.45, 1960.1) * mm, "end": v(2599.32, 1961.26) * mm});
            skArc(sketch, "E278", {"start": v(2599.32, 1961.26) * mm, "mid": v(2595.05, 1962.28) * mm, "end": v(2590.76, 1963.26) * mm});
            skArc(sketch, "E279", {"start": v(2590.76, 1963.26) * mm, "mid": v(2587.82, 1964.04) * mm, "end": v(2584.95, 1965.06) * mm});
            skArc(sketch, "E280", {"start": v(2584.95, 1965.06) * mm, "mid": v(2583.11, 1965.9) * mm, "end": v(2581.39, 1966.95) * mm});
            skArc(sketch, "E281", {"start": v(2581.39, 1966.95) * mm, "mid": v(2577.6, 1971.65) * mm, "end": v(2577.08, 1977.66) * mm});
            skArc(sketch, "E282", {"start": v(2577.08, 1977.66) * mm, "mid": v(2577.45, 1978.94) * mm, "end": v(2578, 1980.15) * mm});
            skArc(sketch, "E283", {"start": v(2578, 1980.15) * mm, "mid": v(2578.53, 1980.94) * mm, "end": v(2579.12, 1981.68) * mm});
            skArc(sketch, "E284", {"start": v(2579.12, 1981.68) * mm, "mid": v(2579.86, 1982.45) * mm, "end": v(2580.67, 1983.14) * mm});
            skArc(sketch, "E285", {"start": v(2580.67, 1983.14) * mm, "mid": v(2582.55, 1984.4) * mm, "end": v(2584.6, 1985.4) * mm});
            skArc(sketch, "E286", {"start": v(2584.6, 1985.4) * mm, "mid": v(2588.99, 1986.67) * mm, "end": v(2593.54, 1987.1) * mm});
            skArc(sketch, "E287", {"start": v(2593.54, 1987.1) * mm, "mid": v(2596.56, 1986.98) * mm, "end": v(2599.57, 1986.62) * mm});
            skArc(sketch, "E288", {"start": v(2599.57, 1986.62) * mm, "mid": v(2601.36, 1986.25) * mm, "end": v(2603.11, 1985.74) * mm});
            skArc(sketch, "E289", {"start": v(2603.11, 1985.74) * mm, "mid": v(2604.73, 1985.12) * mm, "end": v(2606.28, 1984.35) * mm});
            skArc(sketch, "E290", {"start": v(2606.28, 1984.35) * mm, "mid": v(2608.27, 1983.08) * mm, "end": v(2610.1, 1981.57) * mm});
            skArc(sketch, "E291", {"start": v(2610.1, 1981.57) * mm, "mid": v(2615.7, 1981.75) * mm, "end": v(2615.52, 1987.36) * mm});
            skArc(sketch, "E292", {"start": v(2615.52, 1987.36) * mm, "mid": v(2612.95, 1989.5) * mm, "end": v(2610.13, 1991.29) * mm});
            skLineSegment(sketch, "E293", {"start": v(2669.13, 1957.04) * mm, "end": v(2692.1, 1917) * mm});
            skArc(sketch, "E294", {"start": v(2692.1, 1917) * mm, "mid": v(2697.51, 1915.54) * mm, "end": v(2698.98, 1920.95) * mm});
            skLineSegment(sketch, "E295", {"start": v(2698.98, 1920.95) * mm, "end": v(2674.81, 1963.07) * mm});
            skLineSegment(sketch, "E296", {"start": v(2674.81, 1963.07) * mm, "end": v(2697.9, 1987.58) * mm});
            skArc(sketch, "E297", {"start": v(2697.9, 1987.58) * mm, "mid": v(2697.73, 1993.2) * mm, "end": v(2692.12, 1993.03) * mm});
            skLineSegment(sketch, "E298", {"start": v(2692.12, 1993.03) * mm, "end": v(2654.37, 1952.95) * mm});
            skLineSegment(sketch, "E299", {"start": v(2654.37, 1952.95) * mm, "end": v(2654.37, 2025.03) * mm});
            skArc(sketch, "E300", {"start": v(2654.37, 2025.03) * mm, "mid": v(2650.4, 2029) * mm, "end": v(2646.43, 2025.03) * mm});
            skLineSegment(sketch, "E301", {"start": v(2646.43, 2025.03) * mm, "end": v(2646.43, 1918.98) * mm});
            skArc(sketch, "E302", {"start": v(2646.43, 1918.98) * mm, "mid": v(2650.4, 1915.01) * mm, "end": v(2654.37, 1918.98) * mm});
            skLineSegment(sketch, "E303", {"start": v(2654.37, 1918.98) * mm, "end": v(2654.37, 1941.37) * mm});
            skLineSegment(sketch, "E304", {"start": v(2654.37, 1941.37) * mm, "end": v(2669.13, 1957.04) * mm});
            skCircle(sketch, "E305", {"center": v(2792.9, 1972) * mm, "radius": 57 * mm});
            skLineSegment(sketch, "E306", {"start": v(2763.67, 1980.58) * mm, "end": v(2763.67, 1958.45) * mm});
            skLineSegment(sketch, "E307", {"start": v(2763.67, 1958.45) * mm, "end": v(2778.76, 1974.5) * mm});
            skLineSegment(sketch, "E308", {"start": v(2778.76, 1974.5) * mm, "end": v(2763.67, 1980.58) * mm});
            skLineSegment(sketch, "E309", {"start": v(2805.23, 1941.72) * mm, "end": v(2821.54, 1959.07) * mm});
            skLineSegment(sketch, "E310", {"start": v(2821.54, 1959.07) * mm, "end": v(2821.54, 1983.44) * mm});
            skLineSegment(sketch, "E311", {"start": v(2821.54, 1983.44) * mm, "end": v(2805.23, 1966.09) * mm});
            skLineSegment(sketch, "E312", {"start": v(2805.23, 1966.09) * mm, "end": v(2805.23, 1941.72) * mm});
            skLineSegment(sketch, "E313", {"start": v(2802.63, 1969.35) * mm, "end": v(2820.03, 1987.86) * mm});
            skLineSegment(sketch, "E314", {"start": v(2820.03, 1987.86) * mm, "end": v(2782.58, 2002.94) * mm});
            skLineSegment(sketch, "E315", {"start": v(2782.58, 2002.94) * mm, "end": v(2765.18, 1984.42) * mm});
            skLineSegment(sketch, "E316", {"start": v(2765.18, 1984.42) * mm, "end": v(2802.63, 1969.35) * mm});
            skArc(sketch, "E317", {"start": v(2825.1, 1956.84) * mm, "mid": v(2825.52, 1957.5) * mm, "end": v(2825.67, 1958.25) * mm});
            skLineSegment(sketch, "E318", {"start": v(2825.67, 1958.25) * mm, "end": v(2825.67, 1988.65) * mm});
            skArc(sketch, "E319", {"start": v(2825.67, 1988.65) * mm, "mid": v(2825.31, 1989.8) * mm, "end": v(2824.38, 1990.56) * mm});
            skLineSegment(sketch, "E320", {"start": v(2824.38, 1990.56) * mm, "end": v(2782.81, 2007.3) * mm});
            skArc(sketch, "E321", {"start": v(2782.81, 2007.3) * mm, "mid": v(2781.6, 2007.4) * mm, "end": v(2780.54, 2006.79) * mm});
            skLineSegment(sketch, "E322", {"start": v(2780.54, 2006.79) * mm, "end": v(2760.1, 1985.05) * mm});
            skArc(sketch, "E323", {"start": v(2760.1, 1985.05) * mm, "mid": v(2759.69, 1984.4) * mm, "end": v(2759.54, 1983.64) * mm});
            skLineSegment(sketch, "E324", {"start": v(2759.54, 1983.64) * mm, "end": v(2759.54, 1953.24) * mm});
            skArc(sketch, "E325", {"start": v(2759.54, 1953.24) * mm, "mid": v(2760.85, 1951.33) * mm, "end": v(2763.1, 1951.83) * mm});
            skLineSegment(sketch, "E326", {"start": v(2763.1, 1951.83) * mm, "end": v(2782.87, 1972.85) * mm});
            skLineSegment(sketch, "E327", {"start": v(2782.87, 1972.85) * mm, "end": v(2801.1, 1965.51) * mm});
            skLineSegment(sketch, "E328", {"start": v(2801.1, 1965.51) * mm, "end": v(2801.1, 1936.51) * mm});
            skArc(sketch, "E329", {"start": v(2801.1, 1936.51) * mm, "mid": v(2802.4, 1934.6) * mm, "end": v(2804.67, 1935.1) * mm});
            skLineSegment(sketch, "E330", {"start": v(2804.67, 1935.1) * mm, "end": v(2825.1, 1956.84) * mm});
            skCircle(sketch, "E331", {"center": v(2792.9, 1972) * mm, "radius": 52.87 * mm});
            skLineSegment(sketch, "E332", {"start": v(2105, 1044.01) * mm, "end": v(2105, 982.27) * mm});
            skLineSegment(sketch, "E333", {"start": v(2424.83, 982.28) * mm, "end": v(2424.83, 1044.01) * mm});
            skArc(sketch, "E334", {"start": v(691.6, 1578.94) * mm, "mid": v(694.24, 1572.58) * mm, "end": v(700.6, 1569.94) * mm});
            skLineSegment(sketch, "E335", {"start": v(700.6, 1569.94) * mm, "end": v(718.18, 1569.94) * mm});
            skArc(sketch, "E336", {"start": v(718.18, 1569.94) * mm, "mid": v(724.33, 1572.37) * mm, "end": v(727.16, 1578.34) * mm});
            skLineSegment(sketch, "E337", {"start": v(727.16, 1578.34) * mm, "end": v(748.41, 1896.94) * mm});
            skArc(sketch, "E338", {"start": v(748.41, 1896.94) * mm, "mid": v(763.63, 1929.04) * mm, "end": v(796.67, 1942.1) * mm});
            skLineSegment(sketch, "E339", {"start": v(796.67, 1942.1) * mm, "end": v(896.6, 1942.1) * mm});
            skLineSegment(sketch, "E340", {"start": v(896.6, 1942.1) * mm, "end": v(996.53, 1942.1) * mm});
            skArc(sketch, "E341", {"start": v(996.53, 1942.1) * mm, "mid": v(1029.57, 1929.04) * mm, "end": v(1044.79, 1896.94) * mm});
            skLineSegment(sketch, "E342", {"start": v(1044.79, 1896.94) * mm, "end": v(1066.04, 1578.34) * mm});
            skArc(sketch, "E343", {"start": v(1066.04, 1578.34) * mm, "mid": v(1068.87, 1572.37) * mm, "end": v(1075.02, 1569.94) * mm});
            skLineSegment(sketch, "E344", {"start": v(1075.02, 1569.94) * mm, "end": v(1092.6, 1569.94) * mm});
            skArc(sketch, "E345", {"start": v(1092.6, 1569.94) * mm, "mid": v(1098.97, 1572.58) * mm, "end": v(1101.6, 1578.94) * mm});
            skLineSegment(sketch, "E346", {"start": v(1101.6, 1578.94) * mm, "end": v(1101.6, 1864.94) * mm});
            skLineSegment(sketch, "E347", {"start": v(1101.6, 1864.94) * mm, "end": v(1089.26, 1864.94) * mm});
            skArc(sketch, "E348", {"start": v(1089.26, 1864.94) * mm, "mid": v(1083.6, 1864.94) * mm, "end": v(1083.6, 1870.6) * mm});
            skLineSegment(sketch, "E349", {"start": v(1083.6, 1870.6) * mm, "end": v(1083.6, 2009.1) * mm});
            skLineSegment(sketch, "E350", {"start": v(1083.6, 2009.1) * mm, "end": v(709.6, 2009.1) * mm});
            skLineSegment(sketch, "E351", {"start": v(709.6, 2009.1) * mm, "end": v(709.6, 1870.6) * mm});
            skArc(sketch, "E352", {"start": v(709.6, 1870.6) * mm, "mid": v(709.6, 1864.94) * mm, "end": v(703.94, 1864.94) * mm});
            skLineSegment(sketch, "E353", {"start": v(703.94, 1864.94) * mm, "end": v(691.6, 1864.94) * mm});
            skLineSegment(sketch, "E354", {"start": v(691.6, 1864.94) * mm, "end": v(691.6, 1578.94) * mm});
            skCircle(sketch, "E355", {"center": v(1353.82, 1415.07) * mm, "radius": 3 * mm});
            skCircle(sketch, "E356", {"center": v(1236.5, 1109.65) * mm, "radius": 3 * mm});
            skCircle(sketch, "E357", {"center": v(1421.17, 1434.38) * mm, "radius": 3 * mm});
            skCircle(sketch, "E358", {"center": v(1236.5, 1424.41) * mm, "radius": 3 * mm});
            skCircle(sketch, "E359", {"center": v(1296.32, 1144.84) * mm, "radius": 3 * mm});
            skCircle(sketch, "E360", {"center": v(1170.94, 1439.55) * mm, "radius": 3 * mm});
            skCircle(sketch, "E361", {"center": v(1296.32, 1356.02) * mm, "radius": 3 * mm});
            skCircle(sketch, "E362", {"center": v(1170.94, 1094.52) * mm, "radius": 3 * mm});
            skArc(sketch, "E363", {"start": v(1290.32, 1112.84) * mm, "mid": v(1301.48, 1119.88) * mm, "end": v(1305.82, 1132.33) * mm});
            skLineSegment(sketch, "E364", {"start": v(1305.82, 1132.33) * mm, "end": v(1305.82, 1361.8) * mm});
            skArc(sketch, "E365", {"start": v(1305.82, 1361.8) * mm, "mid": v(1313.88, 1385.87) * mm, "end": v(1334.8, 1400.25) * mm});
            skLineSegment(sketch, "E366", {"start": v(1334.8, 1400.25) * mm, "end": v(1443.34, 1431.37) * mm});
            skLineSegment(sketch, "E367", {"start": v(1443.34, 1431.37) * mm, "end": v(1438.38, 1448.68) * mm});
            skLineSegment(sketch, "E368", {"start": v(1438.38, 1448.68) * mm, "end": v(1356.6, 1425.23) * mm});
            skArc(sketch, "E369", {"start": v(1356.6, 1425.23) * mm, "mid": v(1319.18, 1419.47) * mm, "end": v(1281.51, 1423.26) * mm});
            skLineSegment(sketch, "E370", {"start": v(1281.51, 1423.26) * mm, "end": v(1150.46, 1453.52) * mm});
            skLineSegment(sketch, "E371", {"start": v(1150.46, 1453.52) * mm, "end": v(1146.42, 1435.98) * mm});
            skLineSegment(sketch, "E372", {"start": v(1146.42, 1435.98) * mm, "end": v(1203.82, 1422.72) * mm});
            skArc(sketch, "E373", {"start": v(1203.82, 1422.72) * mm, "mid": v(1248.43, 1394.58) * mm, "end": v(1265.82, 1344.77) * mm});
            skLineSegment(sketch, "E374", {"start": v(1265.82, 1344.77) * mm, "end": v(1265.82, 1189.3) * mm});
            skArc(sketch, "E375", {"start": v(1265.82, 1189.3) * mm, "mid": v(1248.43, 1139.5) * mm, "end": v(1203.82, 1111.34) * mm});
            skLineSegment(sketch, "E376", {"start": v(1203.82, 1111.34) * mm, "end": v(1143.2, 1097.35) * mm});
            skLineSegment(sketch, "E377", {"start": v(1143.2, 1097.35) * mm, "end": v(1147.26, 1079.81) * mm});
            skLineSegment(sketch, "E378", {"start": v(1147.26, 1079.81) * mm, "end": v(1290.32, 1112.84) * mm});
            skLineSegment(sketch, "E379", {"start": v(1036.5, 942.03) * mm, "end": v(1054, 942.03) * mm});
            skLineSegment(sketch, "E380", {"start": v(1054, 942.03) * mm, "end": v(1054, 1249.22) * mm});
            skArc(sketch, "E381", {"start": v(1054, 1249.22) * mm, "mid": v(1045.21, 1270.43) * mm, "end": v(1024, 1279.22) * mm});
            skLineSegment(sketch, "E382", {"start": v(1024, 1279.22) * mm, "end": v(710, 1279.22) * mm});
            skArc(sketch, "E383", {"start": v(710, 1279.22) * mm, "mid": v(688.79, 1270.43) * mm, "end": v(680, 1249.22) * mm});
            skLineSegment(sketch, "E384", {"start": v(680, 1249.22) * mm, "end": v(680, 942.03) * mm});
            skLineSegment(sketch, "E385", {"start": v(680, 942.03) * mm, "end": v(697.5, 942.03) * mm});
            skArc(sketch, "E386", {"start": v(697.5, 942.03) * mm, "mid": v(699.62, 941.15) * mm, "end": v(700.5, 939.03) * mm});
            skLineSegment(sketch, "E387", {"start": v(700.5, 939.03) * mm, "end": v(700.5, 919.22) * mm});
            skArc(sketch, "E388", {"start": v(700.5, 919.22) * mm, "mid": v(706.36, 905.08) * mm, "end": v(720.5, 899.22) * mm});
            skLineSegment(sketch, "E389", {"start": v(720.5, 899.22) * mm, "end": v(1013.5, 899.22) * mm});
            skArc(sketch, "E390", {"start": v(1013.5, 899.22) * mm, "mid": v(1027.64, 905.08) * mm, "end": v(1033.5, 919.22) * mm});
            skLineSegment(sketch, "E391", {"start": v(1033.5, 919.22) * mm, "end": v(1033.5, 939.03) * mm});
            skArc(sketch, "E392", {"start": v(1033.5, 939.03) * mm, "mid": v(1034.38, 941.15) * mm, "end": v(1036.5, 942.03) * mm});
            skLineSegment(sketch, "E393", {"start": v(1108.88, 1005.82) * mm, "end": v(1108.88, 950.82) * mm});
            skArc(sketch, "E394", {"start": v(1108.88, 950.82) * mm, "mid": v(1114.74, 936.68) * mm, "end": v(1128.88, 930.82) * mm});
            skLineSegment(sketch, "E395", {"start": v(1128.88, 930.82) * mm, "end": v(1422.88, 930.82) * mm});
            skArc(sketch, "E396", {"start": v(1422.88, 930.82) * mm, "mid": v(1437.02, 936.68) * mm, "end": v(1442.88, 950.82) * mm});
            skLineSegment(sketch, "E397", {"start": v(1442.88, 950.82) * mm, "end": v(1442.88, 1005.82) * mm});
            skArc(sketch, "E398", {"start": v(1442.88, 1005.82) * mm, "mid": v(1437.02, 1019.96) * mm, "end": v(1422.88, 1025.82) * mm});
            skLineSegment(sketch, "E399", {"start": v(1422.88, 1025.82) * mm, "end": v(1128.88, 1025.82) * mm});
            skArc(sketch, "E400", {"start": v(1128.88, 1025.82) * mm, "mid": v(1114.74, 1019.96) * mm, "end": v(1108.88, 1005.82) * mm});
            skLineSegment(sketch, "E401", {"start": v(1034.18, 1299.6) * mm, "end": v(1018.74, 1366.49) * mm});
            skLineSegment(sketch, "E402", {"start": v(1018.74, 1366.49) * mm, "end": v(746.15, 1366.49) * mm});
            skLineSegment(sketch, "E403", {"start": v(746.15, 1366.49) * mm, "end": v(730.7, 1299.6) * mm});
            skLineSegment(sketch, "E404", {"start": v(730.7, 1299.6) * mm, "end": v(740.83, 1297.26) * mm});
            skArc(sketch, "E405", {"start": v(740.83, 1297.26) * mm, "mid": v(746.3, 1297.63) * mm, "end": v(750.62, 1301) * mm});
            skLineSegment(sketch, "E406", {"start": v(750.62, 1301) * mm, "end": v(772.62, 1332.07) * mm});
            skArc(sketch, "E407", {"start": v(772.62, 1332.07) * mm, "mid": v(780.57, 1339) * mm, "end": v(790.8, 1341.49) * mm});
            skLineSegment(sketch, "E408", {"start": v(790.8, 1341.49) * mm, "end": v(882.44, 1341.49) * mm});
            skLineSegment(sketch, "E409", {"start": v(882.44, 1341.49) * mm, "end": v(974.08, 1341.49) * mm});
            skArc(sketch, "E410", {"start": v(974.08, 1341.49) * mm, "mid": v(984.32, 1339) * mm, "end": v(992.27, 1332.07) * mm});
            skLineSegment(sketch, "E411", {"start": v(992.27, 1332.07) * mm, "end": v(1014.26, 1301) * mm});
            skArc(sketch, "E412", {"start": v(1014.26, 1301) * mm, "mid": v(1018.6, 1297.63) * mm, "end": v(1024.05, 1297.26) * mm});
            skLineSegment(sketch, "E413", {"start": v(1024.05, 1297.26) * mm, "end": v(1034.18, 1299.6) * mm});
            skLineSegment(sketch, "E414", {"start": v(733, 1456.47) * mm, "end": v(748.45, 1389.58) * mm});
            skLineSegment(sketch, "E415", {"start": v(748.45, 1389.58) * mm, "end": v(1021.04, 1389.58) * mm});
            skLineSegment(sketch, "E416", {"start": v(1021.04, 1389.58) * mm, "end": v(1036.48, 1456.47) * mm});
            skLineSegment(sketch, "E417", {"start": v(1036.48, 1456.47) * mm, "end": v(1026.35, 1458.8) * mm});
            skArc(sketch, "E418", {"start": v(1026.35, 1458.8) * mm, "mid": v(1020.9, 1458.43) * mm, "end": v(1016.56, 1455.07) * mm});
            skLineSegment(sketch, "E419", {"start": v(1016.56, 1455.07) * mm, "end": v(994.57, 1424) * mm});
            skArc(sketch, "E420", {"start": v(994.57, 1424) * mm, "mid": v(986.62, 1417.07) * mm, "end": v(976.38, 1414.58) * mm});
            skLineSegment(sketch, "E421", {"start": v(976.38, 1414.58) * mm, "end": v(884.74, 1414.58) * mm});
            skLineSegment(sketch, "E422", {"start": v(884.74, 1414.58) * mm, "end": v(793.1, 1414.58) * mm});
            skArc(sketch, "E423", {"start": v(793.1, 1414.58) * mm, "mid": v(782.87, 1417.07) * mm, "end": v(774.92, 1424) * mm});
            skLineSegment(sketch, "E424", {"start": v(774.92, 1424) * mm, "end": v(752.92, 1455.07) * mm});
            skArc(sketch, "E425", {"start": v(752.92, 1455.07) * mm, "mid": v(748.6, 1458.43) * mm, "end": v(743.13, 1458.8) * mm});
            skLineSegment(sketch, "E426", {"start": v(743.13, 1458.8) * mm, "end": v(733, 1456.47) * mm});
            skArc(sketch, "E427", {"start": v(1260.46, 1636.57) * mm, "mid": v(1249.3, 1643.6) * mm, "end": v(1244.95, 1656.05) * mm});
            skLineSegment(sketch, "E428", {"start": v(1244.95, 1656.05) * mm, "end": v(1244.95, 1885.52) * mm});
            skArc(sketch, "E429", {"start": v(1244.95, 1885.52) * mm, "mid": v(1236.9, 1909.6) * mm, "end": v(1215.98, 1923.97) * mm});
            skLineSegment(sketch, "E430", {"start": v(1215.98, 1923.97) * mm, "end": v(1107.44, 1955.1) * mm});
            skLineSegment(sketch, "E431", {"start": v(1107.44, 1955.1) * mm, "end": v(1112.4, 1972.4) * mm});
            skLineSegment(sketch, "E432", {"start": v(1112.4, 1972.4) * mm, "end": v(1194.18, 1948.95) * mm});
            skArc(sketch, "E433", {"start": v(1194.18, 1948.95) * mm, "mid": v(1231.6, 1943.2) * mm, "end": v(1269.27, 1946.98) * mm});
            skLineSegment(sketch, "E434", {"start": v(1269.27, 1946.98) * mm, "end": v(1400.31, 1977.24) * mm});
            skLineSegment(sketch, "E435", {"start": v(1400.31, 1977.24) * mm, "end": v(1404.36, 1959.7) * mm});
            skLineSegment(sketch, "E436", {"start": v(1404.36, 1959.7) * mm, "end": v(1346.96, 1946.45) * mm});
            skArc(sketch, "E437", {"start": v(1346.96, 1946.45) * mm, "mid": v(1302.35, 1918.3) * mm, "end": v(1284.95, 1868.5) * mm});
            skLineSegment(sketch, "E438", {"start": v(1284.95, 1868.5) * mm, "end": v(1284.95, 1713.02) * mm});
            skArc(sketch, "E439", {"start": v(1284.95, 1713.02) * mm, "mid": v(1302.35, 1663.22) * mm, "end": v(1346.96, 1635.07) * mm});
            skLineSegment(sketch, "E440", {"start": v(1346.96, 1635.07) * mm, "end": v(1407.57, 1621.07) * mm});
            skLineSegment(sketch, "E441", {"start": v(1407.57, 1621.07) * mm, "end": v(1403.52, 1603.54) * mm});
            skLineSegment(sketch, "E442", {"start": v(1403.52, 1603.54) * mm, "end": v(1260.46, 1636.57) * mm});
            skCircle(sketch, "E443", {"center": v(1379.84, 1963.27) * mm, "radius": 3 * mm});
            skCircle(sketch, "E444", {"center": v(1314.27, 1948.14) * mm, "radius": 3 * mm});
            skCircle(sketch, "E445", {"center": v(1129.6, 1958.1) * mm, "radius": 3 * mm});
            skCircle(sketch, "E446", {"center": v(1254.45, 1879.74) * mm, "radius": 3 * mm});
            skCircle(sketch, "E447", {"center": v(1254.45, 1668.56) * mm, "radius": 3 * mm});
            skCircle(sketch, "E448", {"center": v(1314.27, 1633.38) * mm, "radius": 3 * mm});
            skCircle(sketch, "E449", {"center": v(1379.84, 1618.24) * mm, "radius": 3 * mm});
            skCircle(sketch, "E450", {"center": v(1196.96, 1938.8) * mm, "radius": 3 * mm});
            skCircle(sketch, "E451", {"center": v(1016.6, 1956.64) * mm, "radius": 3 * mm});
            skCircle(sketch, "E452", {"center": v(776.6, 1995.52) * mm, "radius": 3 * mm});
            skCircle(sketch, "E453", {"center": v(776.6, 1956.64) * mm, "radius": 3 * mm});
            skCircle(sketch, "E454", {"center": v(1016.6, 1995.52) * mm, "radius": 3 * mm});
            skCircle(sketch, "E455", {"center": v(849.9, 1486.18) * mm, "radius": 3 * mm});
            skCircle(sketch, "E456", {"center": v(1089.9, 1525.06) * mm, "radius": 3 * mm});
            skCircle(sketch, "E457", {"center": v(1089.9, 1486.18) * mm, "radius": 3 * mm});
            skCircle(sketch, "E458", {"center": v(849.9, 1525.06) * mm, "radius": 3 * mm});
            skArc(sketch, "E459", {"start": v(1174.9, 1902.75) * mm, "mid": v(1172.27, 1909.12) * mm, "end": v(1165.9, 1911.75) * mm});
            skLineSegment(sketch, "E460", {"start": v(1165.9, 1911.75) * mm, "end": v(1148.32, 1911.75) * mm});
            skArc(sketch, "E461", {"start": v(1148.32, 1911.75) * mm, "mid": v(1142.18, 1909.33) * mm, "end": v(1139.34, 1903.35) * mm});
            skLineSegment(sketch, "E462", {"start": v(1139.34, 1903.35) * mm, "end": v(1118.1, 1584.75) * mm});
            skArc(sketch, "E463", {"start": v(1118.1, 1584.75) * mm, "mid": v(1102.88, 1552.65) * mm, "end": v(1069.84, 1539.6) * mm});
            skLineSegment(sketch, "E464", {"start": v(1069.84, 1539.6) * mm, "end": v(969.9, 1539.6) * mm});
            skLineSegment(sketch, "E465", {"start": v(969.9, 1539.6) * mm, "end": v(869.97, 1539.6) * mm});
            skArc(sketch, "E466", {"start": v(869.97, 1539.6) * mm, "mid": v(836.93, 1552.65) * mm, "end": v(821.72, 1584.75) * mm});
            skLineSegment(sketch, "E467", {"start": v(821.72, 1584.75) * mm, "end": v(800.47, 1903.35) * mm});
            skArc(sketch, "E468", {"start": v(800.47, 1903.35) * mm, "mid": v(797.63, 1909.33) * mm, "end": v(791.49, 1911.75) * mm});
            skLineSegment(sketch, "E469", {"start": v(791.49, 1911.75) * mm, "end": v(773.9, 1911.75) * mm});
            skArc(sketch, "E470", {"start": v(773.9, 1911.75) * mm, "mid": v(767.54, 1909.12) * mm, "end": v(764.9, 1902.75) * mm});
            skLineSegment(sketch, "E471", {"start": v(764.9, 1902.75) * mm, "end": v(764.9, 1616.76) * mm});
            skLineSegment(sketch, "E472", {"start": v(764.9, 1616.76) * mm, "end": v(777.25, 1616.76) * mm});
            skArc(sketch, "E473", {"start": v(777.25, 1616.76) * mm, "mid": v(782.9, 1616.76) * mm, "end": v(782.9, 1611.1) * mm});
            skLineSegment(sketch, "E474", {"start": v(782.9, 1611.1) * mm, "end": v(782.9, 1472.6) * mm});
            skLineSegment(sketch, "E475", {"start": v(782.9, 1472.6) * mm, "end": v(1156.9, 1472.6) * mm});
            skLineSegment(sketch, "E476", {"start": v(1156.9, 1472.6) * mm, "end": v(1156.9, 1611.1) * mm});
            skArc(sketch, "E477", {"start": v(1156.9, 1611.1) * mm, "mid": v(1156.9, 1616.76) * mm, "end": v(1162.56, 1616.76) * mm});
            skLineSegment(sketch, "E478", {"start": v(1162.56, 1616.76) * mm, "end": v(1174.9, 1616.76) * mm});
            skLineSegment(sketch, "E479", {"start": v(1174.9, 1616.76) * mm, "end": v(1174.9, 1902.75) * mm});
            skLineSegment(sketch, "E480", {"start": v(1088.88, 1322.1) * mm, "end": v(1108.88, 1322.1) * mm});
            skLineSegment(sketch, "E481", {"start": v(1108.88, 1322.1) * mm, "end": v(1108.88, 1080.82) * mm});
            skArc(sketch, "E482", {"start": v(1108.88, 1080.82) * mm, "mid": v(1114.74, 1066.68) * mm, "end": v(1128.88, 1060.82) * mm});
            skLineSegment(sketch, "E483", {"start": v(1128.88, 1060.82) * mm, "end": v(1422.88, 1060.82) * mm});
            skArc(sketch, "E484", {"start": v(1422.88, 1060.82) * mm, "mid": v(1437.02, 1066.68) * mm, "end": v(1442.88, 1080.82) * mm});
            skLineSegment(sketch, "E485", {"start": v(1442.88, 1080.82) * mm, "end": v(1442.88, 1322.1) * mm});
            skLineSegment(sketch, "E486", {"start": v(1442.88, 1322.1) * mm, "end": v(1462.88, 1322.1) * mm});
            skLineSegment(sketch, "E487", {"start": v(1462.88, 1322.1) * mm, "end": v(1462.88, 1158.18) * mm});
            skArc(sketch, "E488", {"start": v(1462.88, 1158.18) * mm, "mid": v(1462.88, 1152.53) * mm, "end": v(1468.54, 1152.53) * mm});
            skLineSegment(sketch, "E489", {"start": v(1468.54, 1152.53) * mm, "end": v(1480.88, 1152.53) * mm});
            skLineSegment(sketch, "E490", {"start": v(1480.88, 1152.53) * mm, "end": v(1480.88, 930.82) * mm});
            skArc(sketch, "E491", {"start": v(1480.88, 930.82) * mm, "mid": v(1470.63, 906.07) * mm, "end": v(1445.88, 895.82) * mm});
            skLineSegment(sketch, "E492", {"start": v(1445.88, 895.82) * mm, "end": v(1105.88, 895.82) * mm});
            skArc(sketch, "E493", {"start": v(1105.88, 895.82) * mm, "mid": v(1081.13, 906.07) * mm, "end": v(1070.88, 930.82) * mm});
            skLineSegment(sketch, "E494", {"start": v(1070.88, 930.82) * mm, "end": v(1070.88, 1152.53) * mm});
            skLineSegment(sketch, "E495", {"start": v(1070.88, 1152.53) * mm, "end": v(1083.22, 1152.53) * mm});
            skArc(sketch, "E496", {"start": v(1083.22, 1152.53) * mm, "mid": v(1088.88, 1152.53) * mm, "end": v(1088.88, 1158.18) * mm});
            skLineSegment(sketch, "E497", {"start": v(1088.88, 1158.18) * mm, "end": v(1088.88, 1322.1) * mm});
            skLineSegment(sketch, "E498", {"start": v(-2580, 2029) * mm, "end": v(-1360, 2029) * mm});
            skLineSegment(sketch, "E499", {"start": v(-2560, 2009) * mm, "end": v(-1380, 2009) * mm});
            skLineSegment(sketch, "E500", {"start": v(-2560, -391) * mm, "end": v(-2560, 2009) * mm});
            skLineSegment(sketch, "E501", {"start": v(-2560, 1380.24) * mm, "end": v(-2163.87, 1380.24) * mm, "construction": true});
            skArc(sketch, "E502.MirrorCS", {"start": v(-2446.9, 1345.9) * mm, "mid": v(-2457.13, 1343.4) * mm, "end": v(-2465.08, 1336.48) * mm});
            skArc(sketch, "E503.MirrorCS", {"start": v(-2245.43, 1336.48) * mm, "mid": v(-2253.38, 1343.4) * mm, "end": v(-2263.62, 1345.9) * mm});
            skArc(sketch, "E504.MirrorCS", {"start": v(-2213.65, 1301.67) * mm, "mid": v(-2219.1, 1302.04) * mm, "end": v(-2223.44, 1305.4) * mm});
            skLineSegment(sketch, "E505.MirrorCS", {"start": v(-2203.52, 1304) * mm, "end": v(-2213.65, 1301.67) * mm});
            skLineSegment(sketch, "E506.MirrorCS", {"start": v(-2496.87, 1301.67) * mm, "end": v(-2507, 1304) * mm});
            skArc(sketch, "E507.MirrorCS", {"start": v(-2487.08, 1305.4) * mm, "mid": v(-2491.4, 1302.04) * mm, "end": v(-2496.87, 1301.67) * mm});
            skLineSegment(sketch, "E508.MirrorCS", {"start": v(-2355.26, 1345.9) * mm, "end": v(-2446.9, 1345.9) * mm});
            skLineSegment(sketch, "E509.MirrorCS", {"start": v(-2263.62, 1345.9) * mm, "end": v(-2355.26, 1345.9) * mm});
            skLineSegment(sketch, "E510.MirrorCS", {"start": v(-2223.44, 1305.4) * mm, "end": v(-2245.43, 1336.48) * mm});
            skLineSegment(sketch, "E511.MirrorCS", {"start": v(-2218.96, 1370.9) * mm, "end": v(-2203.52, 1304) * mm});
            skLineSegment(sketch, "E512.MirrorCS", {"start": v(-2491.55, 1370.9) * mm, "end": v(-2218.96, 1370.9) * mm});
            skLineSegment(sketch, "E513.MirrorCS", {"start": v(-2507, 1304) * mm, "end": v(-2491.55, 1370.9) * mm});
            skLineSegment(sketch, "E514.MirrorCS", {"start": v(-2465.08, 1336.48) * mm, "end": v(-2487.08, 1305.4) * mm});
            skSolve(sketch);
        }
        {
            var Q0;
            Q0=makeQuery(id+"F0.imprint","IMPRINT",FACE,{"disambiguationData":[TD([[makeQuery(id+"F0.imprint","IMPRINT",EDGE,{"derivedFrom":sQuery(id+"F0.wireOp",EDGE,"E0")}),1.0]])]});
            var Q1;
            Q1=makeQuery(id+"F0.imprint","IMPRINT",FACE,{"disambiguationData":[TD([[makeQuery(id+"F0.imprint","IMPRINT",EDGE,{"derivedFrom":sQuery(id+"F0.wireOp",EDGE,"E80")}),-1.0]])]});
            var Q2;
            Q2=makeQuery(id+"F0.imprint","IMPRINT",FACE,{"disambiguationData":[TD([[makeQuery(id+"F0.imprint","IMPRINT",EDGE,{"derivedFrom":sQuery(id+"F0.wireOp",EDGE,"E108")}),1.0]])]});
            var Q3;
            Q3=makeQuery(id+"F0.imprint","IMPRINT",FACE,{"disambiguationData":[TD([[makeQuery(id+"F0.imprint","IMPRINT",EDGE,{"derivedFrom":sQuery(id+"F0.wireOp",EDGE,"E21")}),1.0]])]});
            var Q4;
            Q4=makeQuery(id+"F0.imprint","IMPRINT",FACE,{"disambiguationData":[TD([[makeQuery(id+"F0.imprint","IMPRINT",EDGE,{"derivedFrom":sQuery(id+"F0.wireOp",EDGE,"E67")}),1.0]])]});
            var Q5;
            Q5=makeQuery(id+"F0.imprint","IMPRINT",FACE,{"disambiguationData":[TD([[makeQuery(id+"F0.imprint","IMPRINT",EDGE,{"derivedFrom":sQuery(id+"F0.wireOp",EDGE,"E45")}),1.0]])]});
            var Q6;
            Q6=makeQuery(id+"F0.imprint","IMPRINT",FACE,{"disambiguationData":[TD([[makeQuery(id+"F0.imprint","IMPRINT",EDGE,{"derivedFrom":sQuery(id+"F0.wireOp",EDGE,"E59")}),-1.0]])]});
            var Q7;
            Q7=makeQuery(id+"F0.imprint","IMPRINT",FACE,{"disambiguationData":[TD([[makeQuery(id+"F0.imprint","IMPRINT",EDGE,{"derivedFrom":sQuery(id+"F0.wireOp",EDGE,"E506.MirrorCS")}),-1.0]])]});
            var Q8;
            Q8=sQuery(id+"F0.wireOp",EDGE,"E153");
            var Q9;
            Q9=sQuery(id+"F0.wireOp",EDGE,"E157");
            var Q10;
            Q10=sQuery(id+"F0.wireOp",EDGE,"E153");
            extrude(context, id + "F1", {"entities" : qUnion([Q0, Q1, Q2, Q3, Q4, Q5, Q6, Q7]), "surfaceEntities" : qUnion([Q8, Q9, Q10]), "depth" : 18 * mm});
        }
    });
